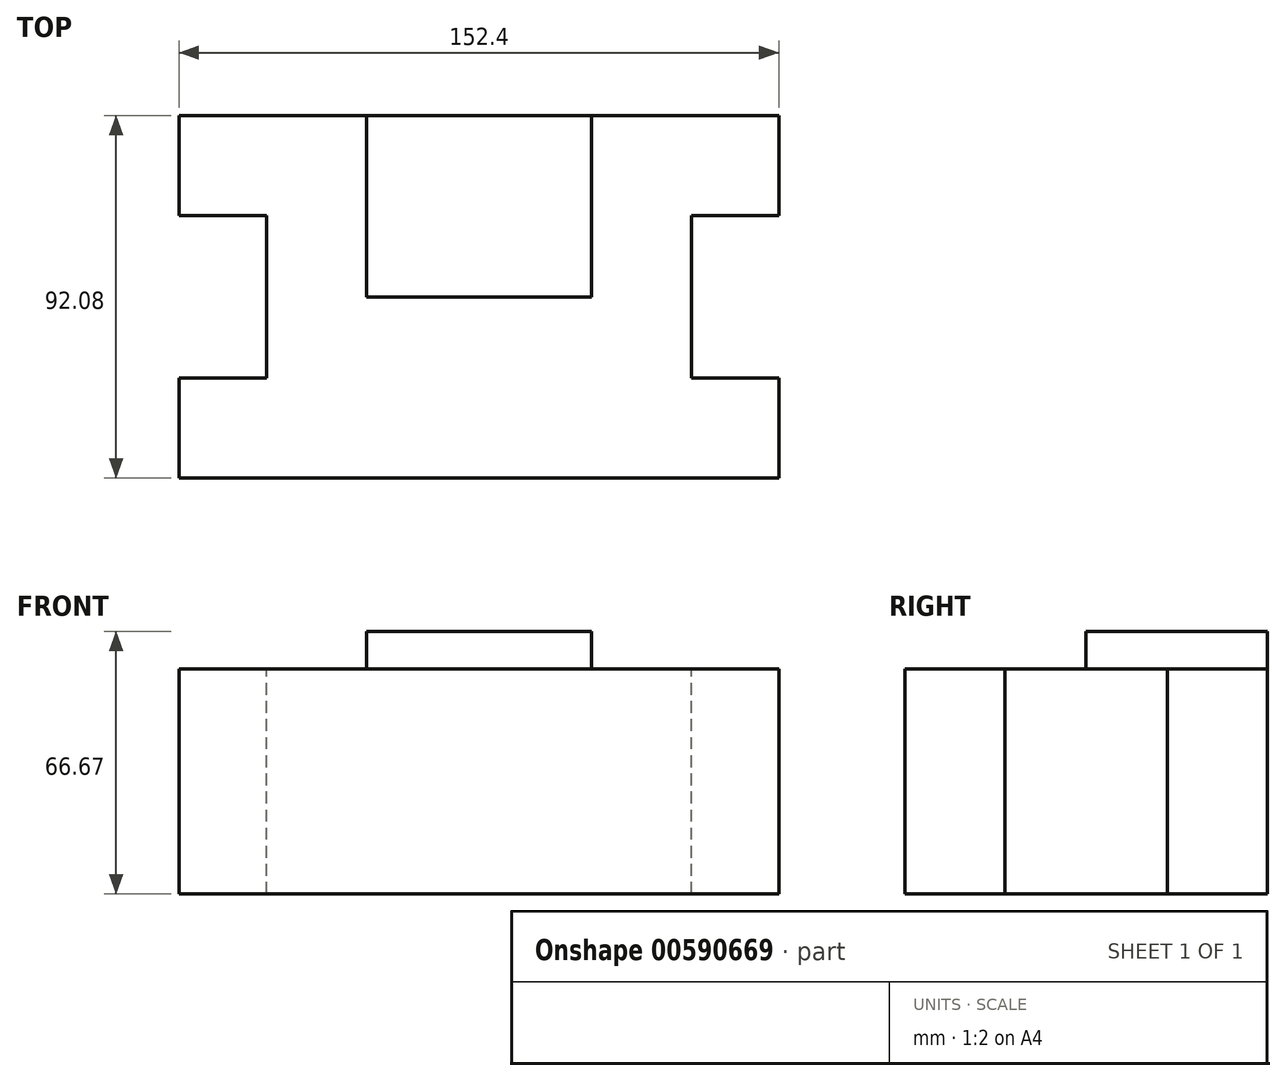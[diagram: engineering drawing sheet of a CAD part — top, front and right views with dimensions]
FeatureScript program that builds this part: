
annotation { "Feature Type Name" : "Feature", "Feature Type Description" : "" }
export const myFeature = defineFeature(function(context is Context, id is Id, definition is map)
    precondition{}
    {
        {
            var Q0;
            Q0=qCreatedBy(makeId("Top.planeOp"),FACE);
            var sketch = newSketch(context, id + "F0", { "sketchPlane" : qUnion([Q0])});
            skLineSegment(sketch, "E0.bottom", {"start": v(76.2, -46.04) * mm, "end": v(-76.2, -46.04) * mm});
            skLineSegment(sketch, "E0.top", {"start": v(76.2, 46.04) * mm, "end": v(-76.2, 46.04) * mm});
            skLineSegment(sketch, "E0.left", {"start": v(76.2, -46.04) * mm, "end": v(76.2, 46.04) * mm});
            skLineSegment(sketch, "E0.right", {"start": v(-76.2, -46.04) * mm, "end": v(-76.2, 46.04) * mm});
            skPoint(sketch, "E0.middle", {"position": v(0, 0) * mm});
            skSolve(sketch);
        }
        {
            var Q0;
            Q0 = qSketchRegion(id + "F0", true);
            extrude(context, id + "F1", {"entities" : qUnion([Q0]), "depth" : 57.15 * mm, "offsetDistance" : 25.4 * mm});
        }
        {
            var Q0;
            Q0=makeQuery(id+"F1.opExtrude","CAP_FACE",FACE,{"disambiguationData":[OSD([sQuery(id+"F0.wireOp",EDGE,"E0.bottom"),sQuery(id+"F0.wireOp",EDGE,"E0.top"),sQuery(id+"F0.wireOp",EDGE,"E0.left"),sQuery(id+"F0.wireOp",EDGE,"E0.right")])],"isStart":false});
            var sketch = newSketch(context, id + "F2", { "sketchPlane" : qUnion([Q0])});
            skLineSegment(sketch, "E1.bottom", {"start": v(-28.57, 46.04) * mm, "end": v(28.58, 46.04) * mm});
            skLineSegment(sketch, "E1.top", {"start": v(-28.57, 0) * mm, "end": v(28.58, 0) * mm});
            skLineSegment(sketch, "E1.left", {"start": v(-28.57, 46.04) * mm, "end": v(-28.57, 0) * mm});
            skLineSegment(sketch, "E1.right", {"start": v(28.58, 46.04) * mm, "end": v(28.58, 0) * mm});
            skSolve(sketch);
        }
        {
            var Q0;
            Q0=makeQuery(id+"F2.imprint","IMPRINT",FACE,{"disambiguationData":[TD([[makeQuery(id+"F2.imprint","IMPRINT",EDGE,{"derivedFrom":sQuery(id+"F2.wireOp",EDGE,"E1.bottom")}),1.0]])]});
            extrude(context, id + "F3", {"entities" : qUnion([Q0]), "operationType" : NewBodyOperationType.ADD, "depth" : 9.52 * mm, "offsetDistance" : 25.4 * mm});
        }
        {
            var Q0;
            Q0=makeQuery(id+"F1.opExtrude","CAP_FACE",FACE,{"disambiguationData":[OSD([sQuery(id+"F0.wireOp",EDGE,"E0.bottom"),sQuery(id+"F0.wireOp",EDGE,"E0.top"),sQuery(id+"F0.wireOp",EDGE,"E0.left"),sQuery(id+"F0.wireOp",EDGE,"E0.right")])],"isStart":false});
            var sketch = newSketch(context, id + "F4", { "sketchPlane" : qUnion([Q0])});
            skLineSegment(sketch, "E2.bottom", {"start": v(-76.2, -20.64) * mm, "end": v(-53.97, -20.64) * mm});
            skLineSegment(sketch, "E2.top", {"start": v(-76.2, 20.64) * mm, "end": v(-53.98, 20.64) * mm});
            skLineSegment(sketch, "E2.left", {"start": v(-76.2, -20.64) * mm, "end": v(-76.2, 20.64) * mm});
            skLineSegment(sketch, "E2.right", {"start": v(-53.97, -20.64) * mm, "end": v(-53.98, 20.64) * mm});
            skLineSegment(sketch, "E3.bottom", {"start": v(76.2, -20.64) * mm, "end": v(53.98, -20.64) * mm});
            skLineSegment(sketch, "E3.top", {"start": v(76.2, 20.64) * mm, "end": v(53.97, 20.64) * mm});
            skLineSegment(sketch, "E3.left", {"start": v(76.2, -20.64) * mm, "end": v(76.2, 20.64) * mm});
            skLineSegment(sketch, "E3.right", {"start": v(53.98, -20.64) * mm, "end": v(53.97, 20.64) * mm});
            skSolve(sketch);
        }
        {
            var Q0;
            Q0 = qSketchRegion(id + "F4", true);
            extrude(context, id + "F5", {"entities" : qUnion([Q0]), "operationType" : NewBodyOperationType.REMOVE, "oppositeDirection" : true, "depth" : 57.15 * mm, "offsetDistance" : 25.4 * mm});
        }
    });
